# Revit family: WBD_Deur_Bu_Dr
name_source: partatom
category: Doors
revit_build: Autodesk Revit Architecture 2013 (Build: 20120221_2030(x64)
units: mm (PartAtom-declared; Revit-internal decimal feet)

## types (1)
- Enkele deur
    3_Delig Aan_Uit = Yes
    A = Yes
    Analytic Construction = <None>
    Assembly Code = B2030110
    B = Yes
    Beslag Nen 5096 R.c. 2 = Yes
    Beslag Nen 5096 R.c. 3 = No
    Beslag Resume 11 = NEN 5096 R.c. 2 mits uitgevoerd conform Attest Kawneer SKG.0055.0292.07.NL (klasse 2)
    Beslag Resume 12 = 3-delige blokscharnieren conform technischhandboek Beslaginbouw hoofdstuk E
    Beslag Resume 13 = Kawneer meerpuntslot SKG** cilinder of krukbediend
    Beslag Resume 14 = A-line handgreep op langschild
    Beslag Resume 15 = Vaste knop op langschild **SKG
    BlokScharnier = Yes
    Brandwerend volgens: = Nen 6069 criteria Ew30 mits uitgevoerd conform:
    Brandwerend volgens:2 = Rapport 2010-Efectis-R0226[Rev.4] Brandbeoordeling EW 30
    Brandwerendheid = Yes
    C = Yes
    CilinderKernTrekBeveiliging = Yes
    D = No
    DIN_Links = Yes
    DIN_Rechts = No
    Default Sill Height = 20 mm  [stored 0.0656168 ft]
    Description = Kawneer RT 62 deurelement volgens productomschrijving:
    Description 2 = Standaard systeemomschrijving RT 62 standaard vlak
    Deurgreep Binnenzijde A_Line = Yes
    Deurgreep Binnenzijde A_Line Verkropt = No
    Deurgreep Binnenzijde Common = No
    Deurgreep Buitenzijde A_Line = No
    Deurgreep Buitenzijde A_Line Verkropt = No
    Deurgreep Buitenzijde Common = No
    Deurgreep Buitenzijde Knop = Yes
    Dikte Stelkozijn = 27 mm  [stored 0.0885827 ft]
    Dikte Stelkozijn onderzijde = 27 mm  [stored 0.0885827 ft]
    DikteStelkozijnOnderzijde_SpelingPui_BuitenbladMWOnderzijde = 17 mm  [stored 0.0557743 ft]
    DikteStelkozijn_SpelingPui_BuitenbladMW = 17 mm  [stored 0.0557743 ft]
    E = No
    F = No
    Function = Exterior
    G = No
    Glasdikte (totaal) = 29 mm  [stored 0.0951444 ft]
    GlassType = Glass, Clear Glazing, Low E
    H = No
    HalveSpouw = 65 mm  [stored 0.213255 ft]
    HalveSpouw_OffsetVkKozijn_Stelkozijn = 79 mm
    Height = 2600 mm  [stored 8.53018 ft]
    I = Yes
    J = No
    K = Yes
    Keynote = 30.33
    Kleur Binnenzijde = Kawneer RAL 9001
    Kleur Binnenzijde Vleugel = Kawneer RAL 9001
    Kleur Buitenzijde = Kawneer RAL 2002
    Kleur Buitenzijde Vleugel = Kawneer RAL 2002
    Kleur H&S = Kawneer Anodiseer kleur RVS-look
    L = No
    M = Yes
    Model = NL-SfB naam
    NL-SfB-Code = 31.25.22
    OffsetVkKozijnVkStelkozijn = 14 mm  [stored 0.0459318 ft]
    Operation = IfcDoor
    Paumelle = No
    RT 52 = No
    RT 62 = Yes
    RT 72 = No
    Speling Pui_ buitenblad MW = 10 mm  [stored 0.0328084 ft]
    Speling Pui_buitenblad MW Onderzijde = 10 mm  [stored 0.0328084 ft]
    Spouwdiepte = 130 mm  [stored 0.426509 ft]
    StelkozijnKleur = Kawneer RAL 9001
    Type Comments = Vrij te parameteriseren Revit Model
    URL = http://www.kawneer.com
    Wall Closure = By host
    Width = 1029 mm  [stored 3.37598 ft]

note: [stored X ft] marks values corroborated as IEEE doubles in the binary element streams (Revit-internal decimal feet)

## geometry (parser evidence)
native form markers: Blend x14, Sweep x26
no freeform markers — native parametric forms only
